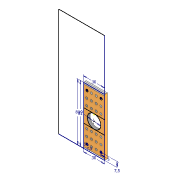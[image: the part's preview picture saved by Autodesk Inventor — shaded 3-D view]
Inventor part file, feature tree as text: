
AUTODESK INVENTOR PART (.ipt)
format: ipt  version: 2020.3 (Build 243373000, 373)  size: 197,120 bytes
history: native  units: mm
features: extrude x4, sketch x3, imported_body x1, pattern_linear x1, fillet x1
ambient origin geometry x8: Origin, YZ Plane, XZ Plane, XY Plane, X Axis, Y Axis, Z Axis, Center Point
bodies: Solid1 (feature_tree)
feature tree (10):
  imported_body  "Base1"
  sketch  "Sketch3"  dims[d21=30.0mm d22=81.0mm]
  extrude  "Extrusion3"  Depth=81.0mm
  extrude  "Extrusion4"  Depth=7.5mm
  pattern_linear  "Rectangular Pattern1"  Spacing1=5.0mm  [1 undecoded]
  sketch  "Sketch4"  dims[d23=5.0mm d24=7.5mm]
  sketch  "Sketch5"  dims[d25=5.0mm d26=0.0mm d27=5.0mm d28=7.5mm d29=10.0mm d30=0.0mm d31=80.0mm d33=9.4mm d34=40.0mm d36=6.7mm d37=30.0mm d38=81.0mm d39=10.0mm d40=0.0mm d41=19.0mm d42=10.0mm d43=0.0mm d44=2.0mm]
  extrude  "Extrusion5"  Depth=2.0mm
  extrude  "Extrusion6"  Depth=10.0mm TaperAngle=0.0deg
  fillet  "Fillet1"  Radius=80.0mm
note: 1 required parameter value undecoded (feature->parameter linkage not recoverable at this tier; creation-order binding heuristic only, values carry confidence <= 0.55)
